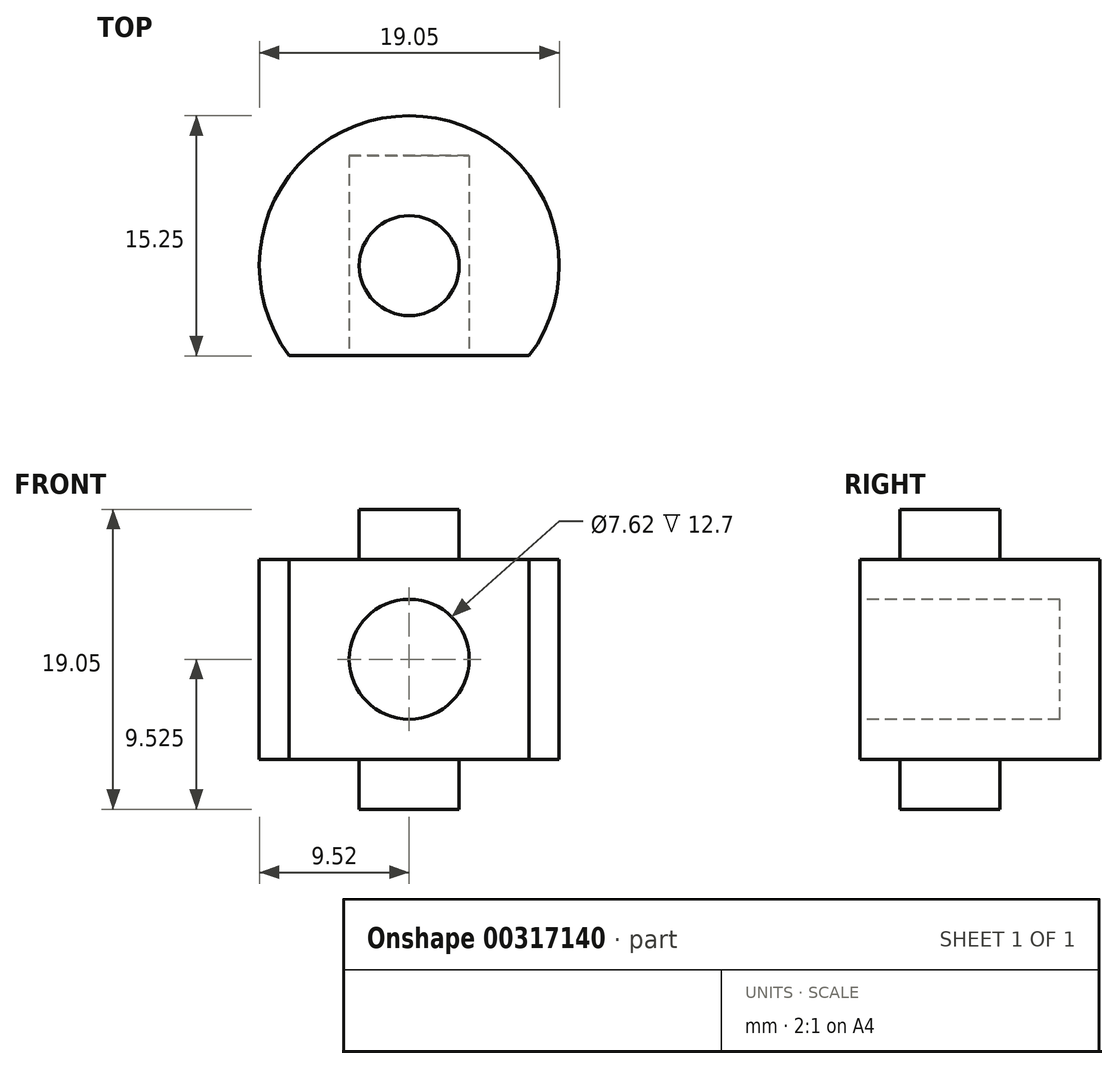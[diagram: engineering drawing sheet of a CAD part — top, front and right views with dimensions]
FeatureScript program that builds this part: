
annotation { "Feature Type Name" : "Feature", "Feature Type Description" : "" }
export const myFeature = defineFeature(function(context is Context, id is Id, definition is map)
    precondition{}
    {
        {
            var Q0;
            Q0=qCreatedBy(makeId("Top.planeOp"),FACE);
            var sketch = newSketch(context, id + "F0", { "sketchPlane" : qUnion([Q0])});
            skCircle(sketch, "E0", {"center": v(0, 0) * mm, "radius": 3.18 * mm});
            skSolve(sketch);
        }
        {
            var Q0;
            Q0=qSketchRegion(id+"F0",true);
            extrude(context, id + "F1", {"entities" : qUnion([Q0]), "depth" : 3.17 * mm});
        }
        {
            var Q0;
            Q0=makeQuery(id+"F1.opExtrude","CAP_FACE",FACE,{"disambiguationData":[OSD([sQuery(id+"F0.wireOp",EDGE,"E0")])],"isStart":false});
            var sketch = newSketch(context, id + "F2", { "sketchPlane" : qUnion([Q0])});
            skCircle(sketch, "E1", {"center": v(0, 0) * mm, "radius": 9.53 * mm});
            skLineSegment(sketch, "E2", {"start": v(7.62, -5.71) * mm, "end": v(-7.62, -5.72) * mm});
            skSolve(sketch);
        }
        {
            var Q0;
            Q0=makeQuery(id+"F2.imprint","IMPRINT",FACE,{"disambiguationData":[TD([[makeQuery(id+"F2.imprint","IMPRINT",EDGE,{"derivedFrom":makeQuery(id+"F1.opExtrude","CAP_EDGE",EDGE,{"disambiguationData":[OSD([sQuery(id+"F0.wireOp",EDGE,"E0")])],"isStart":false})}),1.0]])]});
            var Q1;
            {var subQ0=sQuery(id+"F2.wireOp",EDGE,"E2");Q1=makeQuery(id+"F2.imprint","IMPRINT",FACE,{"disambiguationData":[TD([[makeQuery(id+"F2.imprint","IMPRINT",EDGE,{"derivedFrom":subQ0}),-1.0]])]});}
            extrude(context, id + "F3", {"entities" : qUnion([Q0, Q1]), "operationType" : NewBodyOperationType.ADD, "depth" : 12.7 * mm});
        }
        {
            var Q0;
            Q0=makeQuery(id+"F3.opExtrude","CAP_FACE",FACE,{"disambiguationData":[OSD([sQuery(id+"F2.wireOp",EDGE,"E1")])],"isStart":false});
            var sketch = newSketch(context, id + "F4", { "sketchPlane" : qUnion([Q0])});
            skCircle(sketch, "E3", {"center": v(0, 0) * mm, "radius": 3.18 * mm});
            skSolve(sketch);
        }
        {
            var Q0;
            Q0=qSketchRegion(id+"F4",true);
            extrude(context, id + "F5", {"entities" : qUnion([Q0]), "operationType" : NewBodyOperationType.ADD, "depth" : 3.17 * mm});
        }
        {
            var Q0;
            Q0=makeQuery(id+"F3.opExtrude","SWEPT_FACE",FACE,{"disambiguationData":[OSD([sQuery(id+"F2.wireOp",EDGE,"E2")])]});
            var sketch = newSketch(context, id + "F6", { "sketchPlane" : qUnion([Q0])});
            skCircle(sketch, "E4", {"center": v(0, 9.53) * mm, "radius": 3.81 * mm});
            skPoint(sketch, "E4.centerSnap0", {"position": v(-7.62, 9.53) * mm});
            skPoint(sketch, "E4.centerSnap1", {"position": v(0, 15.88) * mm});
            skSolve(sketch);
        }
        {
            var Q0;
            Q0=qSketchRegion(id+"F6",true);
            extrude(context, id + "F7", {"entities" : qUnion([Q0]), "operationType" : NewBodyOperationType.REMOVE, "oppositeDirection" : true, "depth" : 12.7 * mm});
        }
    });
